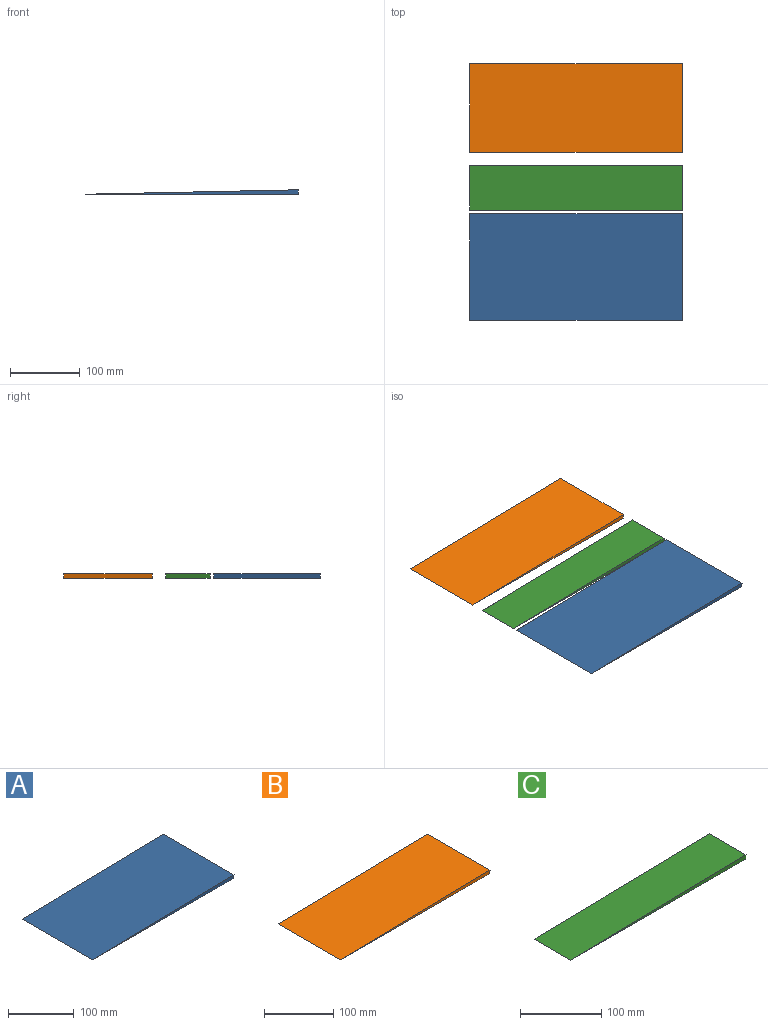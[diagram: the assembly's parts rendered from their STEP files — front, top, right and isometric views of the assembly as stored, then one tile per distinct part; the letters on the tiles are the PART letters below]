
ASSEMBLY  parts=3 mates=4
PART A: 5 faces, bbox 304.8x152.4x6.4 mm
  f0: plane 304.8x152.4mm, normal (0,0,-1), area 46451.5mm2, adj f1,f2,f3,f4
  f1: plane 152.4x6.35mm, normal (1,0,0), area 967.7mm2, adj f0,f2,f3,f4
  f2: plane 304.8x152.4mm, normal (-0.02,0,1), area 46461.6mm2, adj f0,f1,f3,f4
  f3: plane 304.8x6.35mm, normal (0,-1,0), area 967.7mm2, adj f0,f1,f2
  f4: plane 304.8x6.35mm, normal (0,1,0), area 967.7mm2, adj f0,f1,f2
PART B: 5 faces, bbox 304.8x127x6.4 mm
  f0: plane 304.8x127mm, normal (0,0,-1), area 38709.6mm2, adj f1,f2,f3,f4
  f1: plane 127x6.35mm, normal (1,0,0), area 806.5mm2, adj f0,f2,f3,f4
  f2: plane 304.8x127mm, normal (-0.02,0,1), area 38718mm2, adj f0,f1,f3,f4
  f3: plane 304.8x6.35mm, normal (0,-1,0), area 967.7mm2, adj f0,f1,f2
  f4: plane 304.8x6.35mm, normal (0,1,0), area 967.7mm2, adj f0,f1,f2
PART C: 5 faces, bbox 304.8x63.5x6.4 mm
  f0: plane 304.8x63.5mm, normal (0,0,-1), area 19354.8mm2, adj f1,f2,f3,f4
  f1: plane 63.5x6.35mm, normal (1,0,0), area 403.2mm2, adj f0,f2,f3,f4
  f2: plane 304.8x63.5mm, normal (-0.02,0,1), area 19359mm2, adj f0,f1,f3,f4
  f3: plane 304.8x6.35mm, normal (0,-1,0), area 967.7mm2, adj f0,f1,f2
  f4: plane 304.8x6.35mm, normal (0,1,0), area 967.7mm2, adj f0,f1,f2
PLACE A t=(-108.97,-66.52,9.09)mm fixed
PLACE B t=(-108.97,148.56,9.09)mm
PLACE C t=(-108.97,2.51,9.09)mm
MATE planar C.f0 <-> B.f0  axis (0,0,-1) through (-261.37,-29.24,9.09)mm
MATE planar A.f0 <-> C.f0  axis (0,0,-1) through (-261.37,-142.72,9.09)mm
MATE planar C.f1 <-> B.f1  axis (1,0,0) through (-108.97,-29.24,12.27)mm
MATE planar A.f2 <-> C.f2  axis (-0.02,0,1) through (-261.37,-142.72,12.27)mm
